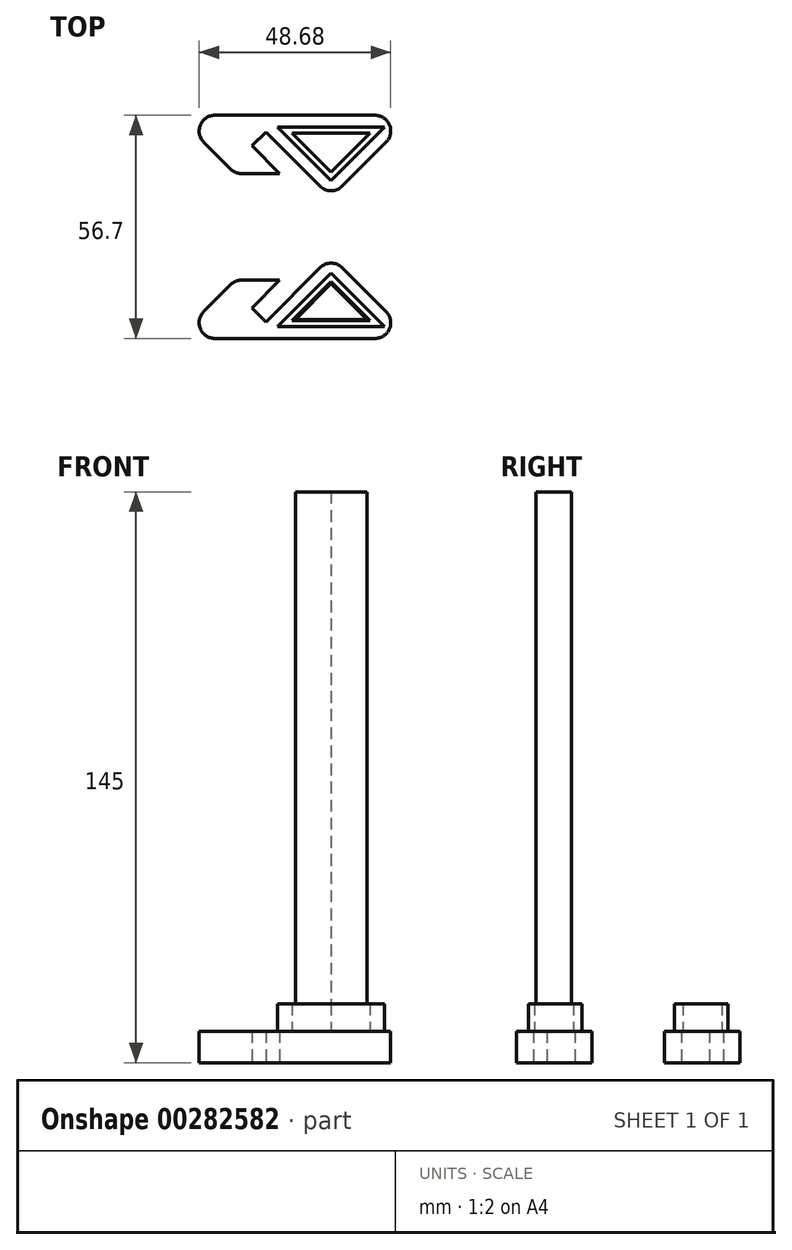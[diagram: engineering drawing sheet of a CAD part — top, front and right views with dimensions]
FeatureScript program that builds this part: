
annotation { "Feature Type Name" : "Feature", "Feature Type Description" : "" }
export const myFeature = defineFeature(function(context is Context, id is Id, definition is map)
    precondition{}
    {
        {
            var Q0;
            Q0=qCreatedBy(makeId("Top.planeOp"),FACE);
            var sketch = newSketch(context, id + "F0", { "sketchPlane" : qUnion([Q0])});
            skLineSegment(sketch, "E0", {"start": v(-9.66, 0) * mm, "end": v(-50.34, 0) * mm});
            skLineSegment(sketch, "E1", {"start": v(-53.17, 6.83) * mm, "end": v(-46.35, 13.65) * mm});
            skLineSegment(sketch, "E2", {"start": v(-43.52, 14.82) * mm, "end": v(-33.86, 14.82) * mm});
            skLineSegment(sketch, "E3", {"start": v(-33.86, 14.82) * mm, "end": v(-40.93, 7.75) * mm});
            skLineSegment(sketch, "E4", {"start": v(-40.93, 7.75) * mm, "end": v(-37.4, 4.22) * mm});
            skLineSegment(sketch, "E5", {"start": v(-37.4, 4.22) * mm, "end": v(-23.64, 17.98) * mm});
            skLineSegment(sketch, "E6", {"start": v(-17.98, 17.98) * mm, "end": v(-6.83, 6.83) * mm});
            skPoint(sketch, "E7.visualSharp", {"position": v(-60, 0) * mm});
            skArc(sketch, "E7.filletArc", {"start": v(-53.17, 6.83) * mm, "mid": v(-54.04, 2.47) * mm, "end": v(-50.34, 0) * mm});
            skPoint(sketch, "E8.visualSharp", {"position": v(0, 0) * mm});
            skArc(sketch, "E8.filletArc", {"start": v(-9.66, 0) * mm, "mid": v(-5.96, 2.47) * mm, "end": v(-6.83, 6.83) * mm});
            skPoint(sketch, "E9.visualSharp", {"position": v(-20.8, 20.8) * mm});
            skArc(sketch, "E9.filletArc", {"start": v(-17.98, 17.98) * mm, "mid": v(-20.8, 19.15) * mm, "end": v(-23.64, 17.98) * mm});
            skPoint(sketch, "E10.visualSharp", {"position": v(-45.18, 14.82) * mm});
            skArc(sketch, "E10.filletArc", {"start": v(-43.52, 14.82) * mm, "mid": v(-45.05, 14.52) * mm, "end": v(-46.35, 13.65) * mm});
            skSolve(sketch);
        }
        {
            var Q0;
            Q0 = qSketchRegion(id + "F0", true);
            extrude(context, id + "F1", {"entities" : qUnion([Q0]), "depth" : 8 * mm});
        }
        {
            var Q0;
            Q0=makeQuery(id+"F1.opExtrude","CAP_FACE",FACE,{"disambiguationData":[OSD([sQuery(id+"F0.wireOp",EDGE,"E0"),sQuery(id+"F0.wireOp",EDGE,"E1"),sQuery(id+"F0.wireOp",EDGE,"E2"),sQuery(id+"F0.wireOp",EDGE,"E3"),sQuery(id+"F0.wireOp",EDGE,"E4"),sQuery(id+"F0.wireOp",EDGE,"E5"),sQuery(id+"F0.wireOp",EDGE,"E6"),sQuery(id+"F0.wireOp",EDGE,"E7.filletArc"),sQuery(id+"F0.wireOp",EDGE,"E8.filletArc"),sQuery(id+"F0.wireOp",EDGE,"E9.filletArc"),sQuery(id+"F0.wireOp",EDGE,"E10.filletArc")])],"isStart":false});
            var sketch = newSketch(context, id + "F2", { "sketchPlane" : qUnion([Q0])});
            skLineSegment(sketch, "E11.0", {"start": v(-7.24, 3) * mm, "end": v(-34.37, 3) * mm});
            skLineSegment(sketch, "E11.1", {"start": v(-20.8, 16.56) * mm, "end": v(-7.24, 3) * mm});
            skLineSegment(sketch, "E11.2", {"start": v(-34.37, 3) * mm, "end": v(-20.8, 16.56) * mm});
            skLineSegment(sketch, "E12.0", {"start": v(-30.75, 4.5) * mm, "end": v(-20.8, 14.44) * mm});
            skLineSegment(sketch, "E12.1", {"start": v(-10.86, 4.5) * mm, "end": v(-30.75, 4.5) * mm});
            skLineSegment(sketch, "E12.2", {"start": v(-20.8, 14.44) * mm, "end": v(-10.86, 4.5) * mm});
            skPoint(sketch, "E13.visualSharp", {"position": v(-20.8, 16.56) * mm});
            skLineSegment(sketch, "E13.filletArc", {"start": v(-20.8, 16.56) * mm, "end": v(-20.8, 16.56) * mm});
            skSolve(sketch);
        }
        {
            var Q0;
            Q0 = qSketchRegion(id + "F2", true);
            extrude(context, id + "F3", {"entities" : qUnion([Q0]), "operationType" : NewBodyOperationType.ADD, "depth" : 7 * mm});
        }
        {
            var Q0;
            Q0=makeQuery(id+"F1.opExtrude","SWEPT_BODY",BODY,{"disambiguationData":[OSD([sQuery(id+"F0.wireOp",EDGE,"E0"),sQuery(id+"F0.wireOp",EDGE,"E1"),sQuery(id+"F0.wireOp",EDGE,"E2"),sQuery(id+"F0.wireOp",EDGE,"E3"),sQuery(id+"F0.wireOp",EDGE,"E4"),sQuery(id+"F0.wireOp",EDGE,"E5"),sQuery(id+"F0.wireOp",EDGE,"E6"),sQuery(id+"F0.wireOp",EDGE,"E7.filletArc"),sQuery(id+"F0.wireOp",EDGE,"E8.filletArc"),sQuery(id+"F0.wireOp",EDGE,"E9.filletArc"),sQuery(id+"F0.wireOp",EDGE,"E10.filletArc")])]});
            transform(context, id + "F4", {"entities" : qUnion([Q0]), "transformType" : TransformType.TRANSLATION_3D, "dx" : 0 * mm, "dy" : -29 * mm, "dz" : 0 * mm, "makeCopy" : true});
        }
        {
            var Q0;
            Q0=makeQuery(id+"F4.opPattern","COPY",BODY,{"derivedFrom":makeQuery(id+"F1.opExtrude","SWEPT_BODY",BODY,{"disambiguationData":[OSD([sQuery(id+"F0.wireOp",EDGE,"E0"),sQuery(id+"F0.wireOp",EDGE,"E1"),sQuery(id+"F0.wireOp",EDGE,"E2"),sQuery(id+"F0.wireOp",EDGE,"E3"),sQuery(id+"F0.wireOp",EDGE,"E4"),sQuery(id+"F0.wireOp",EDGE,"E5"),sQuery(id+"F0.wireOp",EDGE,"E6"),sQuery(id+"F0.wireOp",EDGE,"E7.filletArc"),sQuery(id+"F0.wireOp",EDGE,"E8.filletArc"),sQuery(id+"F0.wireOp",EDGE,"E9.filletArc"),sQuery(id+"F0.wireOp",EDGE,"E10.filletArc")])]}),"instanceName":"1"});
            var Q1;
            Q1=qCreatedBy(makeId("Front.planeOp"),FACE);
            mirror(context, id + "F5", {"entities" : qUnion([Q0]), "mirrorPlane" : qUnion([Q1])});
        }
        {
            var Q0;
            Q0=makeQuery(id+"F4.opPattern","COPY",BODY,{"derivedFrom":makeQuery(id+"F1.opExtrude","SWEPT_BODY",BODY,{"disambiguationData":[OSD([sQuery(id+"F0.wireOp",EDGE,"E0"),sQuery(id+"F0.wireOp",EDGE,"E1"),sQuery(id+"F0.wireOp",EDGE,"E2"),sQuery(id+"F0.wireOp",EDGE,"E3"),sQuery(id+"F0.wireOp",EDGE,"E4"),sQuery(id+"F0.wireOp",EDGE,"E5"),sQuery(id+"F0.wireOp",EDGE,"E6"),sQuery(id+"F0.wireOp",EDGE,"E7.filletArc"),sQuery(id+"F0.wireOp",EDGE,"E8.filletArc"),sQuery(id+"F0.wireOp",EDGE,"E9.filletArc"),sQuery(id+"F0.wireOp",EDGE,"E10.filletArc")])]}),"instanceName":"1"});
            deleteBodies(context, id + "F6", {"entities" : qUnion([Q0])});
        }
        {
            var Q0;
            Q0=makeQuery(id+"F1.opExtrude","SWEPT_BODY",BODY,{"disambiguationData":[OSD([sQuery(id+"F0.wireOp",EDGE,"E0"),sQuery(id+"F0.wireOp",EDGE,"E1"),sQuery(id+"F0.wireOp",EDGE,"E2"),sQuery(id+"F0.wireOp",EDGE,"E3"),sQuery(id+"F0.wireOp",EDGE,"E4"),sQuery(id+"F0.wireOp",EDGE,"E5"),sQuery(id+"F0.wireOp",EDGE,"E6"),sQuery(id+"F0.wireOp",EDGE,"E7.filletArc"),sQuery(id+"F0.wireOp",EDGE,"E8.filletArc"),sQuery(id+"F0.wireOp",EDGE,"E9.filletArc"),sQuery(id+"F0.wireOp",EDGE,"E10.filletArc")])]});
            transform(context, id + "F7", {"entities" : qUnion([Q0]), "transformType" : TransformType.TRANSLATION_3D, "dx" : 0 * mm, "dy" : -27.7 * mm, "dz" : 0 * mm, "makeCopy" : false});
        }
        {
            var Q0;
            Q0=makeQuery(id+"F3.opExtrude","CAP_FACE",FACE,{"disambiguationData":[OSD([sQuery(id+"F2.wireOp",EDGE,"E11.0"),sQuery(id+"F2.wireOp",EDGE,"E11.1"),sQuery(id+"F2.wireOp",EDGE,"E11.2"),sQuery(id+"F2.wireOp",EDGE,"E12.0"),sQuery(id+"F2.wireOp",EDGE,"E12.1"),sQuery(id+"F2.wireOp",EDGE,"E12.2")])],"isStart":false});
            var sketch = newSketch(context, id + "F8", { "sketchPlane" : qUnion([Q0])});
            skLineSegment(sketch, "E14.0", {"start": v(-20.8, -13.75) * mm, "end": v(-11.7, -22.85) * mm});
            skLineSegment(sketch, "E14.1", {"start": v(-29.9, -22.85) * mm, "end": v(-20.8, -13.75) * mm});
            skLineSegment(sketch, "E14.2", {"start": v(-11.7, -22.85) * mm, "end": v(-29.9, -22.85) * mm});
            skSolve(sketch);
        }
        {
            var Q0;
            Q0=makeQuery(id+"F8.imprint","IMPRINT",FACE,{"disambiguationData":[TD([[makeQuery(id+"F8.imprint","IMPRINT",EDGE,{"derivedFrom":sQuery(id+"F8.wireOp",EDGE,"E14.0")}),-1.0]])]});
            extrude(context, id + "F9", {"entities" : qUnion([Q0]), "depth" : 130 * mm});
        }
    });
